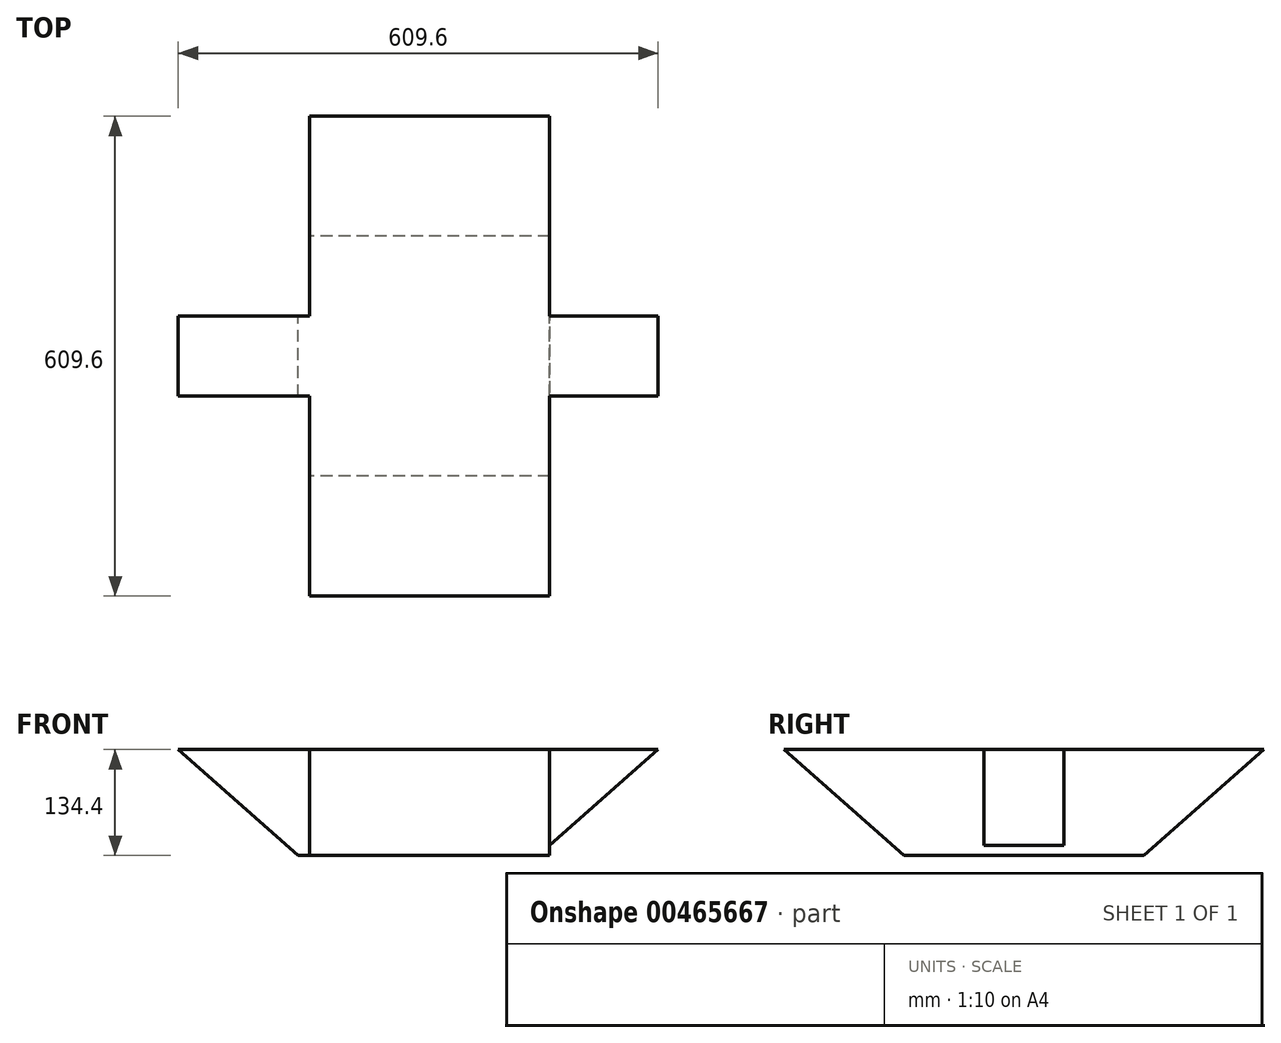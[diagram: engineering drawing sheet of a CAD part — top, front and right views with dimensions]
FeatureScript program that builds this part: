
annotation { "Feature Type Name" : "Feature", "Feature Type Description" : "" }
export const myFeature = defineFeature(function(context is Context, id is Id, definition is map)
    precondition{}
    {
        {
            var Q0;
            Q0=qCreatedBy(makeId("Front.planeOp"),FACE);
            var sketch = newSketch(context, id + "F0", { "sketchPlane" : qUnion([Q0])});
            skLineSegment(sketch, "E0", {"start": v(-319.47, 134.4) * mm, "end": v(290.13, 134.4) * mm});
            skLineSegment(sketch, "E1", {"start": v(-167.07, 0) * mm, "end": v(137.73, 0) * mm});
            skLineSegment(sketch, "E2", {"start": v(-167.07, 0) * mm, "end": v(-319.47, 134.4) * mm});
            skLineSegment(sketch, "E3", {"start": v(137.73, 0) * mm, "end": v(290.13, 134.4) * mm});
            skLineSegment(sketch, "E4", {"start": v(0, 0) * mm, "end": v(0, 134.4) * mm});
            skSolve(sketch);
        }
        {
            var Q0;
            Q0=makeQuery(id+"F0.imprint","IMPRINT",FACE,{"disambiguationData":[TD([[makeQuery(id+"F0.imprint","IMPRINT",EDGE,{"derivedFrom":sQuery(id+"F0.wireOp",EDGE,"E0")}),-1.0]])]});
            extrude(context, id + "F1", {"entities" : qUnion([Q0]), "endBound" : BoundingType.SYMMETRIC, "depth" : 101.6 * mm});
        }
        {
            var Q0;
            Q0=qCreatedBy(makeId("Right.planeOp"),FACE);
            var sketch = newSketch(context, id + "F2", { "sketchPlane" : qUnion([Q0])});
            skLineSegment(sketch, "E5", {"start": v(0, 0) * mm, "end": v(152.4, 0) * mm});
            skLineSegment(sketch, "E6", {"start": v(0, 0) * mm, "end": v(-152.4, 0) * mm});
            skLineSegment(sketch, "E7", {"start": v(0, 0) * mm, "end": v(0, 134.4) * mm});
            skLineSegment(sketch, "E8", {"start": v(0, 134.4) * mm, "end": v(-304.8, 134.4) * mm});
            skLineSegment(sketch, "E9", {"start": v(-304.8, 134.4) * mm, "end": v(-152.4, 0) * mm});
            skLineSegment(sketch, "E10", {"start": v(0, 134.4) * mm, "end": v(304.8, 134.4) * mm});
            skLineSegment(sketch, "E11", {"start": v(304.8, 134.4) * mm, "end": v(152.4, 0) * mm});
            skSolve(sketch);
        }
        {
            var Q0;
            Q0=makeQuery(id+"F2.imprint","IMPRINT",FACE,{"disambiguationData":[TD([[makeQuery(id+"F2.imprint","IMPRINT",EDGE,{"derivedFrom":sQuery(id+"F2.wireOp",EDGE,"E6")}),-1.0]])]});
            var Q1;
            Q1=makeQuery(id+"F2.imprint","IMPRINT",FACE,{"disambiguationData":[TD([[makeQuery(id+"F2.imprint","IMPRINT",EDGE,{"derivedFrom":sQuery(id+"F2.wireOp",EDGE,"E5")}),1.0]])]});
            extrude(context, id + "F3", {"entities" : qUnion([Q0, Q1]), "operationType" : NewBodyOperationType.ADD, "endBound" : BoundingType.SYMMETRIC, "depth" : 304.8 * mm});
        }
    });
